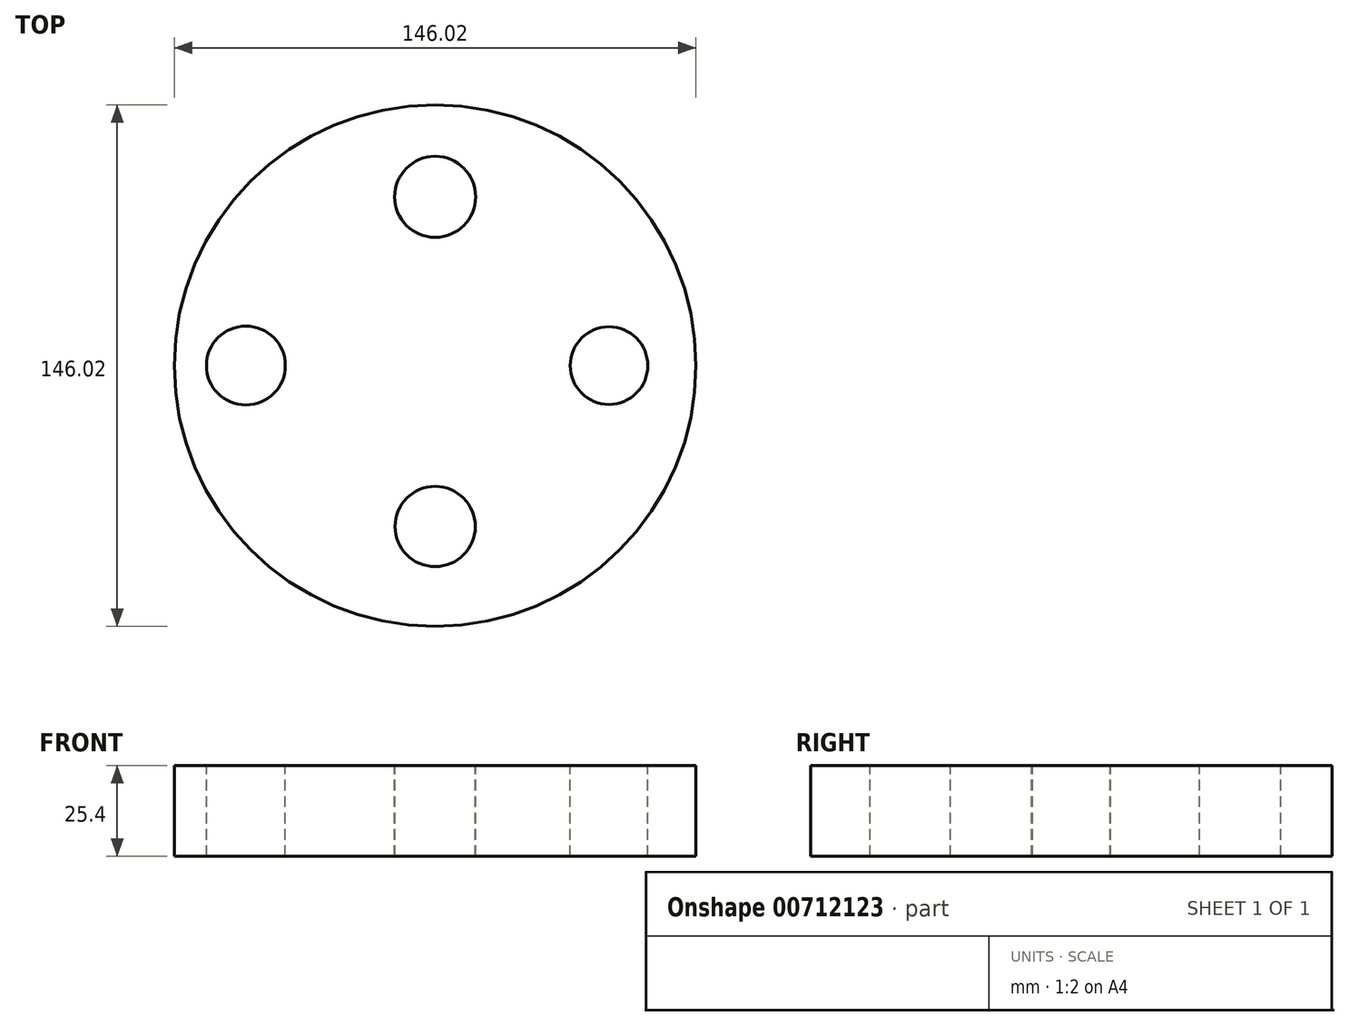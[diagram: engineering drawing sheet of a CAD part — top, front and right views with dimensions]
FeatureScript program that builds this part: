
annotation { "Feature Type Name" : "Feature", "Feature Type Description" : "" }
export const myFeature = defineFeature(function(context is Context, id is Id, definition is map)
    precondition{}
    {
        {
            var Q0;
            Q0=qCreatedBy(makeId("Top.planeOp"),FACE);
            var sketch = newSketch(context, id + "F0", { "sketchPlane" : qUnion([Q0])});
            skCircle(sketch, "E0", {"center": v(0, 0) * mm, "radius": 73 * mm});
            skSolve(sketch);
        }
        {
            var Q0;
            Q0=qCreatedBy(makeId("Top.planeOp"),FACE);
            var sketch = newSketch(context, id + "F1", { "sketchPlane" : qUnion([Q0])});
            skCircle(sketch, "E1", {"center": v(0, 47.27) * mm, "radius": 11.34 * mm});
            skSolve(sketch);
        }
        {
            var Q0;
            Q0=qCreatedBy(makeId("Top.planeOp"),FACE);
            var sketch = newSketch(context, id + "F2", { "sketchPlane" : qUnion([Q0])});
            skCircle(sketch, "E2", {"center": v(48.66, 0) * mm, "radius": 10.86 * mm});
            skSolve(sketch);
        }
        {
            var Q0;
            Q0=qCreatedBy(makeId("Top.planeOp"),FACE);
            var sketch = newSketch(context, id + "F3", { "sketchPlane" : qUnion([Q0])});
            skCircle(sketch, "E3", {"center": v(-52.97, 0) * mm, "radius": 11.05 * mm});
            skSolve(sketch);
        }
        {
            var Q0;
            Q0=qCreatedBy(makeId("Top.planeOp"),FACE);
            var sketch = newSketch(context, id + "F4", { "sketchPlane" : qUnion([Q0])});
            skCircle(sketch, "E4", {"center": v(0, -45.07) * mm, "radius": 11.23 * mm});
            skSolve(sketch);
        }
        {
            var Q0;
            Q0=sQuery(id+"F2.wireOp",EDGE,"E2");
            extrude(context, id + "F5", {"bodyType" : ToolBodyType.SURFACE, "surfaceEntities" : qUnion([Q0]), "depth" : 25.4 * mm, "offsetDistance" : 25.4 * mm});
        }
        {
            var Q0;
            Q0=sQuery(id+"F4.wireOp",EDGE,"E4");
            var Q1;
            Q1=sQuery(id+"F3.wireOp",EDGE,"E3");
            var Q2;
            Q2=sQuery(id+"F1.wireOp",EDGE,"E1");
            extrude(context, id + "F6", {"bodyType" : ToolBodyType.SURFACE, "surfaceEntities" : qUnion([Q0, Q1, Q2]), "depth" : 25.4 * mm, "offsetDistance" : 25.4 * mm});
        }
        {
            var Q0;
            Q0=sQuery(id+"F0.wireOp",EDGE,"E0");
            extrude(context, id + "F7", {"bodyType" : ToolBodyType.SURFACE, "surfaceEntities" : qUnion([Q0]), "depth" : 25.4 * mm, "offsetDistance" : 25.4 * mm});
        }
    });
